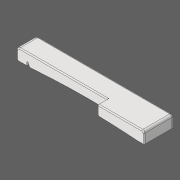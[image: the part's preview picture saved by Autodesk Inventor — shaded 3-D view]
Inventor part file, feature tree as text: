
AUTODESK INVENTOR PART (.ipt)
format: ipt  version: 2020 (Build 240168000, 168)  size: 307,712 bytes
history: native  units: in
note: dims shown in document units (in); Inventor stores cm internally (conversion verified against a paired STEP export)
features: other x4, extrude x4, fillet x2
ambient origin geometry x8: Origin, YZ Plane, XZ Plane, XY Plane, X Axis, Y Axis, Z Axis, Center Point
bodies: Solid1 (feature_tree)
feature tree (10):
  other  "EKey0"
  other  "Slot Start Plane"
  other  "Key Profile"
  extrude  "Upper (u)"  TaperAngle=0.0deg  [1 undecoded]
  extrude  "Lower (d)"  TaperAngle=0.0deg  [1 undecoded]
  extrude  "Protrusion Cutout"  Depth=0.0591in
  fillet  "Front Fillet"  Radius=0.1374in
  extrude  "Slot"  [1 undecoded]
  fillet  "Edge Softening"  Radius=0.0787in
  other  "Slot Sketch"
note: 3 required parameter values undecoded (feature->parameter linkage not recoverable at this tier; creation-order binding heuristic only, values carry confidence <= 0.55)
